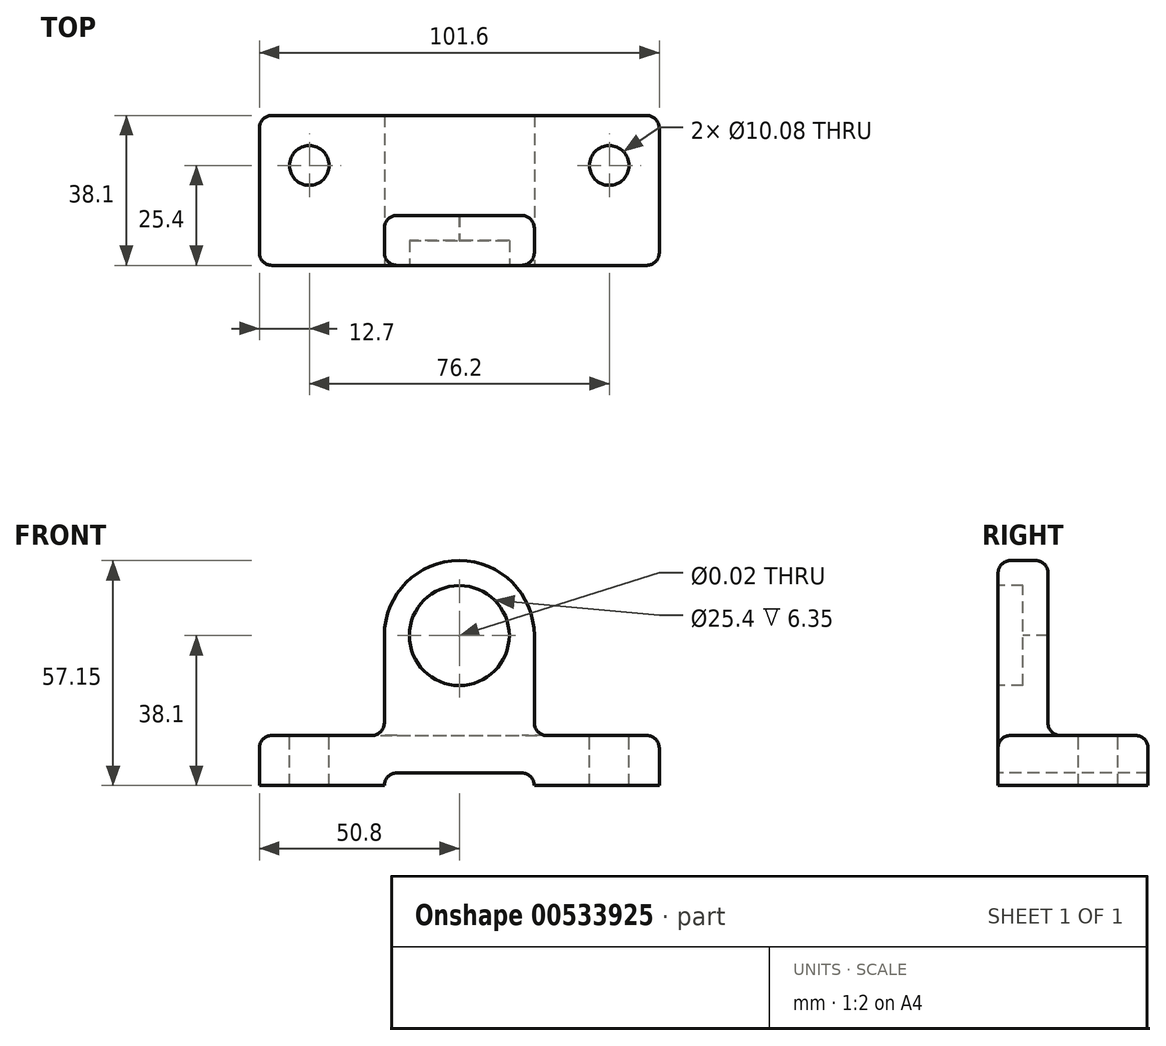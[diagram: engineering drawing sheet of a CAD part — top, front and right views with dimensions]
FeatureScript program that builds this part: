
annotation { "Feature Type Name" : "Feature", "Feature Type Description" : "" }
export const myFeature = defineFeature(function(context is Context, id is Id, definition is map)
    precondition{}
    {
        {
            var Q0;
            Q0=qCreatedBy(makeId("Top.planeOp"),FACE);
            var sketch = newSketch(context, id + "F0", { "sketchPlane" : qUnion([Q0])});
            skLineSegment(sketch, "E0.bottom", {"start": v(0, 0) * mm, "end": v(101.6, 0) * mm});
            skLineSegment(sketch, "E0.top", {"start": v(0, 38.1) * mm, "end": v(101.6, 38.1) * mm});
            skLineSegment(sketch, "E0.left", {"start": v(0, 0) * mm, "end": v(0, 38.1) * mm});
            skLineSegment(sketch, "E0.right", {"start": v(101.6, 0) * mm, "end": v(101.6, 38.1) * mm});
            skSolve(sketch);
        }
        {
            var Q0;
            Q0 = qSketchRegion(id + "F0", true);
            extrude(context, id + "F1", {"entities" : qUnion([Q0]), "depth" : 12.7 * mm, "offsetDistance" : 25.4 * mm});
        }
        {
            var Q0;
            Q0=makeQuery(id+"F1.opExtrude","SWEPT_FACE",FACE,{"disambiguationData":[OSD([sQuery(id+"F0.wireOp",EDGE,"E0.bottom")])]});
            var sketch = newSketch(context, id + "F2", { "sketchPlane" : qUnion([Q0])});
            skLineSegment(sketch, "E1", {"start": v(31.75, 0) * mm, "end": v(31.75, 38.1) * mm});
            skArc(sketch, "E2", {"start": v(69.85, 38.1) * mm, "mid": v(50.8, 57.15) * mm, "end": v(31.75, 38.1) * mm});
            skLineSegment(sketch, "E3", {"start": v(69.85, 38.1) * mm, "end": v(69.85, 0) * mm});
            skSolve(sketch);
        }
        {
            var Q0;
            {var subQ0=sQuery(id+"F2.wireOp",EDGE,"E2");Q0=makeQuery(id+"F2.imprint","IMPRINT",FACE,{"disambiguationData":[TD([[makeQuery(id+"F2.imprint","IMPRINT",EDGE,{"derivedFrom":subQ0}),1.0]])]});}
            var Q1;
            {var subQ0=sQuery(id+"F2.wireOp",EDGE,"E1");var subQ1=sQuery(id+"F0.wireOp",EDGE,"E0.bottom");var subQ2=makeQuery(id+"F1.opExtrude","CAP_EDGE",EDGE,{"disambiguationData":[OSD([subQ1])],"isStart":true});var subQ3=makeQuery(id+"F2.imprint","INTERSECT",VERTEX,{"derivedFrom":[subQ2,subQ0]});Q1=makeQuery(id+"F2.imprint","IMPRINT",FACE,{"disambiguationData":[TD([[makeQuery(id+"F2.imprint","IMPRINT",EDGE,{"disambiguationData":[TD([[subQ3,-1.0]])],"derivedFrom":subQ0}),-1.0]])]});}
            extrude(context, id + "F3", {"entities" : qUnion([Q0, Q1]), "operationType" : NewBodyOperationType.ADD, "oppositeDirection" : true, "depth" : 12.7 * mm, "offsetDistance" : 25.4 * mm});
        }
        {
            var Q0;
            Q0=sQuery(id+"F2.wireOp",VERTEX,"E2.center");
            var Q1;
            Q1=makeQuery(id+"F1.opExtrude","SWEPT_BODY",BODY,{"disambiguationData":[OSD([sQuery(id+"F0.wireOp",EDGE,"E0.bottom"),sQuery(id+"F0.wireOp",EDGE,"E0.top"),sQuery(id+"F0.wireOp",EDGE,"E0.left"),sQuery(id+"F0.wireOp",EDGE,"E0.right")])]});
            hole(context, id + "F4", {"style" : HoleStyle.C_BORE, "endStyle" : HoleEndStyle.THROUGH, "standardTappedOrClearance" : lookupTablePath({ "standard" : "ANSI", "size" : "15/32 (0.47)", "type" : "Drilled" }), "standardBlindInLast" : lookupTablePath({ "standard" : "ANSI", "size" : "15/32", "type" : "Drilled" }), "holeDiameter" : 15 / 812.8 * mm, "cBoreDiameter" : 25.4 * mm, "cBoreDepth" : 6.35 * mm, "isTappedThrough" : true, "tappedDepth" : 12.7 * mm, "tapClearance" : 3, "locations" : qUnion([Q0]), "scope" : qUnion([Q1])});
        }
        {
            var Q0;
            {var subQ0=sQuery(id+"F2.wireOp",EDGE,"E1");var subQ1=sQuery(id+"F0.wireOp",EDGE,"E0.bottom");var subQ2=makeQuery(id+"F1.opExtrude","CAP_EDGE",EDGE,{"disambiguationData":[OSD([subQ1])],"isStart":true});var subQ3=makeQuery(id+"F2.imprint","INTERSECT",VERTEX,{"derivedFrom":[subQ2,subQ0]});Q0=makeQuery(id+"F2.imprint","IMPRINT",FACE,{"disambiguationData":[TD([[makeQuery(id+"F2.imprint","IMPRINT",EDGE,{"disambiguationData":[TD([[subQ3,-1.0]])],"derivedFrom":subQ0}),-1.0]])]});}
            var sketch = newSketch(context, id + "F5", { "sketchPlane" : qUnion([Q0])});
            skLineSegment(sketch, "E4", {"start": v(31.75, 3.18) * mm, "end": v(31.75, 0) * mm});
            skLineSegment(sketch, "E5", {"start": v(69.85, 3.18) * mm, "end": v(69.85, 0) * mm});
            skLineSegment(sketch, "E6", {"start": v(31.75, 0) * mm, "end": v(69.85, 0) * mm});
            skLineSegment(sketch, "E7", {"start": v(69.85, 3.18) * mm, "end": v(31.75, 3.18) * mm});
            skSolve(sketch);
        }
        {
            var Q0;
            Q0 = qSketchRegion(id + "F5", true);
            extrude(context, id + "F6", {"entities" : qUnion([Q0]), "operationType" : NewBodyOperationType.REMOVE, "endBound" : BoundingType.THROUGH_ALL, "oppositeDirection" : true, "depth" : 25.4 * mm, "offsetDistance" : 25.4 * mm});
        }
        {
            var Q0;
            Q0=makeQuery(id+"F1.opExtrude","CAP_FACE",FACE,{"disambiguationData":[OSD([sQuery(id+"F0.wireOp",EDGE,"E0.bottom"),sQuery(id+"F0.wireOp",EDGE,"E0.top"),sQuery(id+"F0.wireOp",EDGE,"E0.left"),sQuery(id+"F0.wireOp",EDGE,"E0.right")])],"isStart":false});
            var sketch = newSketch(context, id + "F7", { "sketchPlane" : qUnion([Q0])});
            skCircle(sketch, "E8", {"center": v(12.7, 25.4) * mm, "radius": 6.99 * mm});
            skCircle(sketch, "E9", {"center": v(88.9, 25.4) * mm, "radius": 6.99 * mm});
            skSolve(sketch);
        }
        {
            var Q0;
            Q0=sQuery(id+"F7.wireOp",VERTEX,"E8.center");
            var Q1;
            Q1=makeQuery(id+"F1.opExtrude","SWEPT_BODY",BODY,{"disambiguationData":[OSD([sQuery(id+"F0.wireOp",EDGE,"E0.bottom"),sQuery(id+"F0.wireOp",EDGE,"E0.top"),sQuery(id+"F0.wireOp",EDGE,"E0.left"),sQuery(id+"F0.wireOp",EDGE,"E0.right")])]});
            hole(context, id + "F8", {"style" : HoleStyle.SIMPLE, "endStyle" : HoleEndStyle.THROUGH, "standardTappedOrClearance" : lookupTablePath({ "standard" : "ANSI", "fit" : "Normal (ASME)", "size" : "3/8", "type" : "Clearance" }), "standardBlindInLast" : lookupTablePath({ "fit" : "Free", "standard" : "ANSI", "size" : "3/8", "type" : "Clearance" }), "holeDiameter" : 10.08 * mm, "isTappedThrough" : true, "tappedDepth" : 12.7 * mm, "tapClearance" : 3, "locations" : qUnion([Q0]), "scope" : qUnion([Q1])});
        }
        {
            var Q0;
            Q0=sQuery(id+"F7.wireOp",VERTEX,"E9.center");
            var Q1;
            Q1=makeQuery(id+"F1.opExtrude","SWEPT_BODY",BODY,{"disambiguationData":[OSD([sQuery(id+"F0.wireOp",EDGE,"E0.bottom"),sQuery(id+"F0.wireOp",EDGE,"E0.top"),sQuery(id+"F0.wireOp",EDGE,"E0.left"),sQuery(id+"F0.wireOp",EDGE,"E0.right")])]});
            hole(context, id + "F9", {"style" : HoleStyle.SIMPLE, "endStyle" : HoleEndStyle.THROUGH, "standardTappedOrClearance" : lookupTablePath({ "standard" : "ANSI", "fit" : "Normal (ASME)", "size" : "3/8", "type" : "Clearance" }), "standardBlindInLast" : lookupTablePath({ "fit" : "Free", "standard" : "ANSI", "size" : "3/8", "type" : "Clearance" }), "holeDiameter" : 10.08 * mm, "isTappedThrough" : true, "tappedDepth" : 12.7 * mm, "tapClearance" : 3, "locations" : qUnion([Q0]), "scope" : qUnion([Q1])});
        }
        {
            var Q0;
            Q0=makeQuery(id+"F1.opExtrude","SWEPT_EDGE",EDGE,{"disambiguationData":[OSD([sQuery(id+"F0.wireOp",EDGE,"E0.bottom"),sQuery(id+"F0.wireOp",EDGE,"E0.right")])]});
            var Q1;
            Q1=makeQuery(id+"F1.opExtrude","SWEPT_EDGE",EDGE,{"disambiguationData":[OSD([sQuery(id+"F0.wireOp",EDGE,"E0.bottom"),sQuery(id+"F0.wireOp",EDGE,"E0.left")])]});
            var Q2;
            Q2=makeQuery(id+"F1.opExtrude","SWEPT_EDGE",EDGE,{"disambiguationData":[OSD([sQuery(id+"F0.wireOp",EDGE,"E0.top"),sQuery(id+"F0.wireOp",EDGE,"E0.left")])]});
            var Q3;
            Q3=makeQuery(id+"F1.opExtrude","SWEPT_EDGE",EDGE,{"disambiguationData":[OSD([sQuery(id+"F0.wireOp",EDGE,"E0.top"),sQuery(id+"F0.wireOp",EDGE,"E0.right")])]});
            fillet(context, id + "F10", {"entities" : qUnion([Q0, Q1, Q2, Q3]), "radius" : 3.17 * mm, "tangentPropagation" : true, "allowEdgeOverflow" : false});
        }
        {
            var Q0;
            Q0=makeQuery(id+"F3.opExtrude","CAP_EDGE",EDGE,{"disambiguationData":[OSD([sQuery(id+"F2.wireOp",EDGE,"E3")])],"isStart":false});
            var Q1;
            Q1=makeQuery(id+"F3.opExtrude","CAP_EDGE",EDGE,{"disambiguationData":[OSD([sQuery(id+"F2.wireOp",EDGE,"E2")])],"isStart":false});
            var Q2;
            Q2=makeQuery(id+"F3.opExtrude","CAP_EDGE",EDGE,{"disambiguationData":[OSD([sQuery(id+"F2.wireOp",EDGE,"E1")])],"isStart":false});
            var Q3;
            {var subQ0=sQuery(id+"F0.wireOp",EDGE,"E0.bottom");Q3=makeQuery(id+"F3.boolean.opBoolean","INTERSECT",EDGE,{"derivedFrom":[makeQuery(id+"F1.opExtrude","CAP_FACE",FACE,{"disambiguationData":[OSD([subQ0,sQuery(id+"F0.wireOp",EDGE,"E0.top"),sQuery(id+"F0.wireOp",EDGE,"E0.left"),sQuery(id+"F0.wireOp",EDGE,"E0.right")])],"isStart":false}),makeQuery(id+"F3.opExtrude","CAP_FACE",FACE,{"disambiguationData":[OSD([subQ0,sQuery(id+"F2.wireOp",EDGE,"E1"),sQuery(id+"F2.wireOp",EDGE,"E2"),sQuery(id+"F2.wireOp",EDGE,"E3")])],"isStart":false})]});}
            var Q4;
            {var subQ1=sQuery(id+"F0.wireOp",EDGE,"E0.left");var subQ2=sQuery(id+"F0.wireOp",EDGE,"E0.bottom");Q4=makeQuery(id+"F3.boolean.opBoolean","SPLIT",EDGE,{"disambiguationData":[TD([makeQuery(id+"F1.opExtrude","SWEPT_FACE",FACE,{"disambiguationData":[OSD([subQ1])]})])],"derivedFrom":makeQuery(id+"F1.opExtrude","CAP_EDGE",EDGE,{"disambiguationData":[OSD([subQ2])],"isStart":false})});}
            var Q5;
            Q5=makeQuery(id+"F1.opExtrude","CAP_EDGE",EDGE,{"disambiguationData":[OSD([sQuery(id+"F0.wireOp",EDGE,"E0.top")])],"isStart":false});
            var Q6;
            Q6=makeQuery(id+"F1.opExtrude","CAP_EDGE",EDGE,{"disambiguationData":[OSD([sQuery(id+"F0.wireOp",EDGE,"E0.left")])],"isStart":false});
            var Q7;
            Q7=makeQuery(id+"F1.opExtrude","CAP_EDGE",EDGE,{"disambiguationData":[OSD([sQuery(id+"F0.wireOp",EDGE,"E0.right")])],"isStart":false});
            var Q8;
            {var subQ0=sQuery(id+"F0.wireOp",EDGE,"E0.right");var subQ1=sQuery(id+"F0.wireOp",EDGE,"E0.bottom");Q8=makeQuery(id+"F3.boolean.opBoolean","SPLIT",EDGE,{"disambiguationData":[TD([makeQuery(id+"F1.opExtrude","SWEPT_FACE",FACE,{"disambiguationData":[OSD([subQ0])]})])],"derivedFrom":makeQuery(id+"F1.opExtrude","CAP_EDGE",EDGE,{"disambiguationData":[OSD([subQ1])],"isStart":false})});}
            var Q9;
            Q9=makeQuery(id+"F3.opExtrude","CAP_EDGE",EDGE,{"disambiguationData":[OSD([sQuery(id+"F2.wireOp",EDGE,"E3")])],"isStart":true});
            var Q10;
            Q10=makeQuery(id+"F3.opExtrude","CAP_EDGE",EDGE,{"disambiguationData":[OSD([sQuery(id+"F2.wireOp",EDGE,"E1")])],"isStart":true});
            var Q11;
            Q11=makeQuery(id+"F3.opExtrude","CAP_EDGE",EDGE,{"disambiguationData":[OSD([sQuery(id+"F2.wireOp",EDGE,"E2")])],"isStart":true});
            var Q12;
            Q12=makeQuery(id+"F3.boolean.opBoolean","INTERSECT",EDGE,{"derivedFrom":[makeQuery(id+"F1.opExtrude","CAP_FACE",FACE,{"disambiguationData":[OSD([sQuery(id+"F0.wireOp",EDGE,"E0.bottom"),sQuery(id+"F0.wireOp",EDGE,"E0.top"),sQuery(id+"F0.wireOp",EDGE,"E0.left"),sQuery(id+"F0.wireOp",EDGE,"E0.right")])],"isStart":false}),makeQuery(id+"F3.opExtrude","SWEPT_FACE",FACE,{"disambiguationData":[OSD([sQuery(id+"F2.wireOp",EDGE,"E1")])]})]});
            var Q13;
            Q13=makeQuery(id+"F3.boolean.opBoolean","INTERSECT",EDGE,{"derivedFrom":[makeQuery(id+"F1.opExtrude","CAP_FACE",FACE,{"disambiguationData":[OSD([sQuery(id+"F0.wireOp",EDGE,"E0.bottom"),sQuery(id+"F0.wireOp",EDGE,"E0.top"),sQuery(id+"F0.wireOp",EDGE,"E0.left"),sQuery(id+"F0.wireOp",EDGE,"E0.right")])],"isStart":false}),makeQuery(id+"F3.opExtrude","SWEPT_FACE",FACE,{"disambiguationData":[OSD([sQuery(id+"F2.wireOp",EDGE,"E3")])]})]});
            var Q14;
            {var subQ0=sQuery(id+"F0.wireOp",EDGE,"E0.left");var subQ1=sQuery(id+"F0.wireOp",EDGE,"E0.top");Q14=makeQuery(id+"F10.opFillet","BLEND_EDGE",EDGE,{"blendedFrom":[makeQuery(id+"F1.opExtrude","SWEPT_EDGE",EDGE,{"disambiguationData":[OSD([subQ1,subQ0])]}),makeQuery(id+"F1.opExtrude","CAP_FACE",FACE,{"disambiguationData":[OSD([sQuery(id+"F0.wireOp",EDGE,"E0.bottom"),subQ1,subQ0,sQuery(id+"F0.wireOp",EDGE,"E0.right")])],"isStart":false})],"blendedInto":[makeQuery(id+"F1.opExtrude","CAP_FACE",FACE,{"disambiguationData":[OSD([sQuery(id+"F0.wireOp",EDGE,"E0.bottom"),subQ1,subQ0,sQuery(id+"F0.wireOp",EDGE,"E0.right")])],"isStart":false})]});}
            var Q15;
            {var subQ0=sQuery(id+"F0.wireOp",EDGE,"E0.left");var subQ1=sQuery(id+"F0.wireOp",EDGE,"E0.bottom");Q15=makeQuery(id+"F10.opFillet","BLEND_EDGE",EDGE,{"blendedFrom":[makeQuery(id+"F1.opExtrude","SWEPT_EDGE",EDGE,{"disambiguationData":[OSD([subQ1,subQ0])]}),makeQuery(id+"F1.opExtrude","CAP_FACE",FACE,{"disambiguationData":[OSD([subQ1,sQuery(id+"F0.wireOp",EDGE,"E0.top"),subQ0,sQuery(id+"F0.wireOp",EDGE,"E0.right")])],"isStart":false})],"blendedInto":[makeQuery(id+"F1.opExtrude","CAP_FACE",FACE,{"disambiguationData":[OSD([subQ1,sQuery(id+"F0.wireOp",EDGE,"E0.top"),subQ0,sQuery(id+"F0.wireOp",EDGE,"E0.right")])],"isStart":false})]});}
            var Q16;
            {var subQ0=sQuery(id+"F0.wireOp",EDGE,"E0.right");var subQ1=sQuery(id+"F0.wireOp",EDGE,"E0.top");Q16=makeQuery(id+"F10.opFillet","BLEND_EDGE",EDGE,{"blendedFrom":[makeQuery(id+"F1.opExtrude","SWEPT_EDGE",EDGE,{"disambiguationData":[OSD([subQ1,subQ0])]}),makeQuery(id+"F1.opExtrude","CAP_FACE",FACE,{"disambiguationData":[OSD([sQuery(id+"F0.wireOp",EDGE,"E0.bottom"),subQ1,sQuery(id+"F0.wireOp",EDGE,"E0.left"),subQ0])],"isStart":false})],"blendedInto":[makeQuery(id+"F1.opExtrude","CAP_FACE",FACE,{"disambiguationData":[OSD([sQuery(id+"F0.wireOp",EDGE,"E0.bottom"),subQ1,sQuery(id+"F0.wireOp",EDGE,"E0.left"),subQ0])],"isStart":false})]});}
            fillet(context, id + "F11", {"entities" : qUnion([Q0, Q1, Q2, Q3, Q4, Q5, Q6, Q7, Q8, Q9, Q10, Q11, Q12, Q13, Q14, Q15, Q16]), "radius" : 3.17 * mm, "tangentPropagation" : true, "allowEdgeOverflow" : false});
        }
        {
            var Q0;
            Q0=makeQuery(id+"F6.boolean.opBoolean","COPY",EDGE,{"derivedFrom":makeQuery(id+"F6.opExtrude","SWEPT_EDGE",EDGE,{"disambiguationData":[OSD([sQuery(id+"F2.wireOp",EDGE,"E1"),sQuery(id+"F5.wireOp",EDGE,"E4"),sQuery(id+"F5.wireOp",EDGE,"E7")])]})});
            var Q1;
            Q1=makeQuery(id+"F6.boolean.opBoolean","COPY",EDGE,{"derivedFrom":makeQuery(id+"F6.opExtrude","SWEPT_EDGE",EDGE,{"disambiguationData":[OSD([sQuery(id+"F2.wireOp",EDGE,"E3"),sQuery(id+"F5.wireOp",EDGE,"E5"),sQuery(id+"F5.wireOp",EDGE,"E7")])]})});
            fillet(context, id + "F12", {"entities" : qUnion([Q0, Q1]), "radius" : 3.17 * mm, "tangentPropagation" : true, "allowEdgeOverflow" : false});
        }
    });
